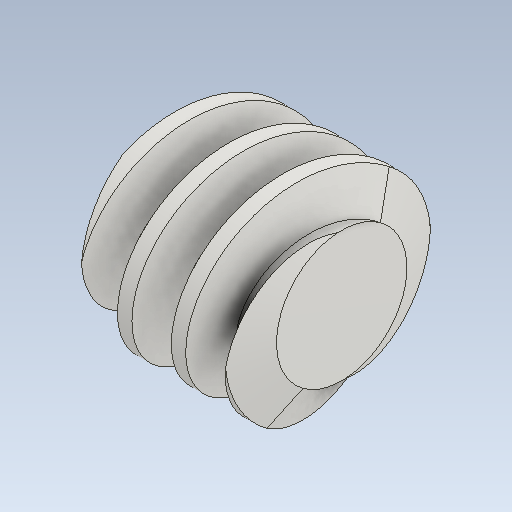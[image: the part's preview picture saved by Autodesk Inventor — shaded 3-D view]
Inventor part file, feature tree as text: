
AUTODESK INVENTOR PART (.ipt)
format: ipt  version: 2021 (Build 250183000, 183)  size: 293,888 bytes
history: native  units: mm (DEFAULTED — no unit token found)
features: other x6, chamfer x2, pattern_circular x2, extrude x1, sketch x1
ambient origin geometry x6: Origin, XZ Plane, X Axis, Y Axis, Z Axis, Center Point
bodies: Solid1 (feature_tree)
feature tree (12):
  extrude  "Base Body"  Depth=10.0mm
  chamfer  "Chamfer1"  Distance=40.0mm
  chamfer  "Chamfer2"  [1 undecoded]
  other  "Tooth Sketch"
  other  "Tooth"
  pattern_circular  "Tooth Pattern"  [2 undecoded]
  other  "Left Tooth"
  pattern_circular  "Left Tooth Pattern"  [2 undecoded]
  other  "Base Body Sketch"
  sketch  "Sketch5"  dims[d4=40.0mm d5=48.0mm d6=40.0mm d7=0.0mm d8=3.202938mm d9=8.8mm d10=3.202938mm d11=8.8mm d12=19.198622mm d14=3.1425mm d24=19.198622mm d25=31.415927mm d26=3.141593mm d27=15.2mm d28=20.0mm d29=24.24mm d30=25.132741mm d31=10.0mm d32=60.0mm d33=0.0mm d34=90.0deg d35=90.0deg d36=0.0mm d37=0.0mm d44=20.0mm d46=360.0deg d47=45.0deg d48=45.0deg d49=68.0168mm d50=0.0mm d54=0.0mm d56=0.0mm d59=40.0mm d60=10.0mm d61=0.0mm d62=25.132741mm d63=10.0mm d64=60.0mm d65=0.0mm d66=90.0deg d67=90.0deg d68=0.0mm d69=0.0mm d70=10.0mm d71=10.0mm d72=20.0mm d73=360.0deg d75=10.0mm d76=10.0mm d77=0.0mm d79=68.0168mm d80=0.0mm]
  other  "Srf1"
  other  "Pitch Diameter"
note: 5 required parameter values undecoded (feature->parameter linkage not recoverable at this tier; creation-order binding heuristic only, values carry confidence <= 0.55)
